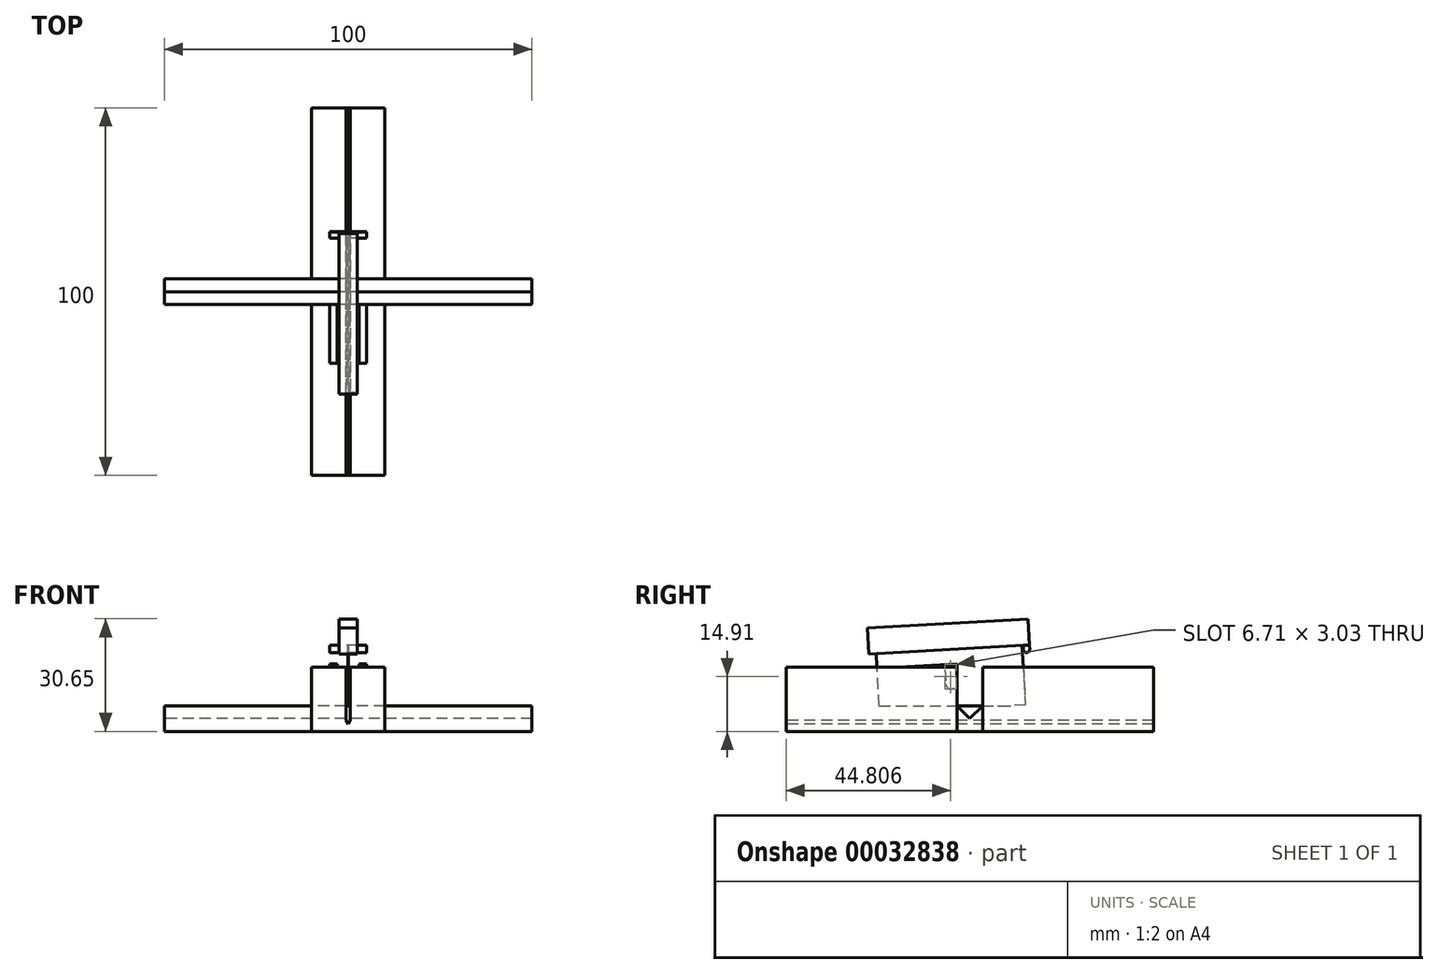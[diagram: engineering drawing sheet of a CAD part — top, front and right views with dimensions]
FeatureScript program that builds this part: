
annotation { "Feature Type Name" : "Feature", "Feature Type Description" : "" }
export const myFeature = defineFeature(function(context is Context, id is Id, definition is map)
    precondition{}
    {
        {
            var Q0;
            Q0=qCreatedBy(makeId("Right.planeOp"),FACE);
            var sketch = newSketch(context, id + "F0", { "sketchPlane" : qUnion([Q0])});
            skLineSegment(sketch, "E0.rect.bottom", {"start": v(3.5, 3.5) * mm, "end": v(-3.5, 3.5) * mm});
            skLineSegment(sketch, "E0.rect.top", {"start": v(3.5, -3.5) * mm, "end": v(-3.5, -3.5) * mm});
            skLineSegment(sketch, "E0.rect.left", {"start": v(3.5, 3.5) * mm, "end": v(3.5, -3.5) * mm});
            skLineSegment(sketch, "E0.rect.right", {"start": v(-3.5, 3.5) * mm, "end": v(-3.5, -3.5) * mm});
            skPoint(sketch, "E0.rect.middle", {"position": v(0, 0) * mm});
            skLineSegment(sketch, "E1", {"start": v(3.5, 3.5) * mm, "end": v(0, 0) * mm});
            skLineSegment(sketch, "E2", {"start": v(-3.5, 3.5) * mm, "end": v(0, 0) * mm});
            skCircle(sketch, "E3", {"center": v(0, 1.68) * mm, "radius": 1.2 * mm, "construction": true});
            skCircle(sketch, "E4", {"center": v(0, 3.54) * mm, "radius": 2.5 * mm, "construction": true});
            skSolve(sketch);
        }
        {
            var Q0;
            Q0=makeQuery(id+"F0.imprint","IMPRINT",FACE,{"disambiguationData":[TD([[makeQuery(id+"F0.imprint","IMPRINT",EDGE,{"derivedFrom":sQuery(id+"F0.wireOp",EDGE,"E0.rect.top")}),-1.0]])]});
            extrude(context, id + "F1", {"entities" : qUnion([Q0]), "endBound" : BoundingType.SYMMETRIC, "depth" : 100 * mm});
        }
        {
            var Q0;
            Q0=qCreatedBy(makeId("Front.planeOp"),FACE);
            var sketch = newSketch(context, id + "F2", { "sketchPlane" : qUnion([Q0])});
            skLineSegment(sketch, "E5.0", {"start": v(50, -3.5) * mm, "end": v(-50, -3.5) * mm});
            skLineSegment(sketch, "E6.bottom", {"start": v(-34.76, -3.5) * mm, "end": v(-25.26, -3.5) * mm});
            skLineSegment(sketch, "E6.top", {"start": v(-34.76, 13.07) * mm, "end": v(-25.26, 13.07) * mm});
            skLineSegment(sketch, "E6.left", {"start": v(-34.76, -3.5) * mm, "end": v(-34.76, 13.07) * mm});
            skLineSegment(sketch, "E6.right", {"start": v(-25.26, -3.5) * mm, "end": v(-25.26, 13.07) * mm});
            skSolve(sketch);
        }
        {
            var Q0;
            Q0=qCreatedBy(makeId("Right.planeOp"),FACE);
            var sketch = newSketch(context, id + "F3", { "sketchPlane" : qUnion([Q0])});
            skLineSegment(sketch, "E7", {"start": v(-24.54, 1.5) * mm, "end": v(-25.62, 20.82) * mm});
            skLineSegment(sketch, "E8", {"start": v(-25.62, 20.82) * mm, "end": v(14.06, 23.04) * mm});
            skLineSegment(sketch, "E9", {"start": v(14.06, 23.04) * mm, "end": v(15.14, 3.72) * mm});
            skLineSegment(sketch, "E10", {"start": v(15.14, 3.72) * mm, "end": v(-24.54, 1.5) * mm});
            skLineSegment(sketch, "E11", {"start": v(-24.54, 1.5) * mm, "end": v(25.1, 1.5) * mm});
            skCircle(sketch, "E12", {"center": v(-5.3, 13.36) * mm, "radius": 1.41 * mm});
            skCircle(sketch, "E13", {"center": v(-5.09, 9.46) * mm, "radius": 1.41 * mm});
            skLineSegment(sketch, "E14", {"start": v(-6.71, 13.28) * mm, "end": v(-6.5, 9.38) * mm});
            skLineSegment(sketch, "E15", {"start": v(-3.9, 13.44) * mm, "end": v(-3.68, 9.54) * mm});
            skLineSegment(sketch, "E16", {"start": v(-5.78, 21.93) * mm, "end": v(-4.7, 2.61) * mm, "construction": true});
            skLineSegment(sketch, "E17", {"start": v(-27.84, 24.7) * mm, "end": v(-27.44, 17.58) * mm});
            skLineSegment(sketch, "E18", {"start": v(-27.44, 17.58) * mm, "end": v(16.23, 20.03) * mm});
            skLineSegment(sketch, "E19", {"start": v(16.23, 20.03) * mm, "end": v(15.83, 27.15) * mm});
            skLineSegment(sketch, "E20", {"start": v(15.83, 27.15) * mm, "end": v(-27.84, 24.7) * mm});
            skSolve(sketch);
        }
        {
            var Q0;
            {var subQ9=sQuery(id+"F3.wireOp",EDGE,"E10");Q0=makeQuery(id+"F3.imprint","IMPRINT",FACE,{"disambiguationData":[TD([[makeQuery(id+"F3.imprint","IMPRINT",EDGE,{"derivedFrom":subQ9}),-1.0]])]});}
            extrude(context, id + "F4", {"entities" : qUnion([Q0]), "endBound" : BoundingType.SYMMETRIC, "depth" : .22 * mm});
        }
        {
            var Q0;
            {var subQ5=sQuery(id+"F3.wireOp",EDGE,"E8");Q0=makeQuery(id+"F3.imprint","IMPRINT",FACE,{"disambiguationData":[TD([[makeQuery(id+"F3.imprint","IMPRINT",EDGE,{"derivedFrom":subQ5}),-1.0]])]});}
            extrude(context, id + "F5", {"entities" : qUnion([Q0]), "operationType" : NewBodyOperationType.ADD, "endBound" : BoundingType.SYMMETRIC, "depth" : 1.15 * mm});
        }
        {
            var Q0;
            {var subQ7=sQuery(id+"F3.wireOp",EDGE,"E8");Q0=makeQuery(id+"F3.imprint","IMPRINT",FACE,{"disambiguationData":[TD([[makeQuery(id+"F3.imprint","IMPRINT",EDGE,{"derivedFrom":subQ7}),1.0]])]});}
            extrude(context, id + "F6", {"entities" : qUnion([Q0]), "endBound" : BoundingType.SYMMETRIC, "depth" : 5 * mm});
        }
        {
            var Q0;
            Q0=makeQuery(id+"F5.opExtrude","CAP_FACE",FACE,{"disambiguationData":[OSD([sQuery(id+"F3.wireOp",EDGE,"E7"),sQuery(id+"F3.wireOp",EDGE,"E8"),sQuery(id+"F3.wireOp",EDGE,"E9"),sQuery(id+"F3.wireOp",EDGE,"E18")])],"isStart":true});
            var Q1;
            Q1=makeQuery(id+"F6.opExtrude","CAP_FACE",FACE,{"disambiguationData":[OSD([sQuery(id+"F3.wireOp",EDGE,"E7"),sQuery(id+"F3.wireOp",EDGE,"E8"),sQuery(id+"F3.wireOp",EDGE,"E9"),sQuery(id+"F3.wireOp",EDGE,"E17"),sQuery(id+"F3.wireOp",EDGE,"E18"),sQuery(id+"F3.wireOp",EDGE,"E19"),sQuery(id+"F3.wireOp",EDGE,"E20")])],"isStart":true});
            extrude(context, id + "F7", {"entities" : qUnion([Q0]), "operationType" : NewBodyOperationType.ADD, "endBound" : BoundingType.UP_TO_SURFACE, "endBoundEntityFace" : qUnion([Q1]), "depth" : 25 * mm});
        }
        {
            var Q0;
            Q0=makeQuery(id+"F5.opExtrude","CAP_FACE",FACE,{"disambiguationData":[OSD([sQuery(id+"F3.wireOp",EDGE,"E7"),sQuery(id+"F3.wireOp",EDGE,"E8"),sQuery(id+"F3.wireOp",EDGE,"E9"),sQuery(id+"F3.wireOp",EDGE,"E18")])],"isStart":false});
            var Q1;
            Q1=makeQuery(id+"F6.opExtrude","CAP_FACE",FACE,{"disambiguationData":[OSD([sQuery(id+"F3.wireOp",EDGE,"E7"),sQuery(id+"F3.wireOp",EDGE,"E8"),sQuery(id+"F3.wireOp",EDGE,"E9"),sQuery(id+"F3.wireOp",EDGE,"E17"),sQuery(id+"F3.wireOp",EDGE,"E18"),sQuery(id+"F3.wireOp",EDGE,"E19"),sQuery(id+"F3.wireOp",EDGE,"E20")])],"isStart":false});
            extrude(context, id + "F8", {"entities" : qUnion([Q0]), "operationType" : NewBodyOperationType.ADD, "endBound" : BoundingType.UP_TO_SURFACE, "endBoundEntityFace" : qUnion([Q1]), "depth" : 25 * mm});
        }
        {
            var Q0;
            Q0=qCreatedBy(makeId("Front.planeOp"),FACE);
            var sketch = newSketch(context, id + "F9", { "sketchPlane" : qUnion([Q0])});
            skLineSegment(sketch, "E21.bottom", {"start": v(-0.61, 3.5) * mm, "end": v(0.6, 3.5) * mm});
            skLineSegment(sketch, "E21.top", {"start": v(-0.6, -1.5) * mm, "end": v(0.61, -1.5) * mm});
            skLineSegment(sketch, "E21.left", {"start": v(-0.61, 3.5) * mm, "end": v(-0.6, -1.5) * mm});
            skLineSegment(sketch, "E21.right", {"start": v(0.6, 3.5) * mm, "end": v(0.61, -1.5) * mm});
            skLineSegment(sketch, "E22", {"start": v(0, -1.5) * mm, "end": v(-0.6, -0.5) * mm});
            skLineSegment(sketch, "E23", {"start": v(0, -1.5) * mm, "end": v(0.61, -0.5) * mm});
            skSolve(sketch);
        }
        {
            var Q0;
            Q0=makeQuery(id+"F9.imprint","IMPRINT",FACE,{"disambiguationData":[TD([[makeQuery(id+"F9.imprint","IMPRINT",EDGE,{"derivedFrom":sQuery(id+"F9.wireOp",EDGE,"E21.bottom")}),-1.0]])]});
            var Q1;
            Q1=sQuery(id+"F9.wireOp",EDGE,"E21.left");
            extrude(context, id + "F10", {"entities" : qUnion([Q0]), "operationType" : NewBodyOperationType.REMOVE, "surfaceEntities" : qUnion([Q1]), "endBound" : BoundingType.THROUGH_ALL, "oppositeDirection" : true, "depth" : 25 * mm, "hasSecondDirection" : true, "secondDirectionBound" : SecondDirectionBoundingType.THROUGH_ALL, "secondDirectionOppositeDirection" : false, "secondDirectionDepth" : 25 * mm});
        }
        {
            var Q0;
            Q0=qCreatedBy(makeId("Right.planeOp"),FACE);
            var sketch = newSketch(context, id + "F11", { "sketchPlane" : qUnion([Q0])});
            skLineSegment(sketch, "E24.0", {"start": v(3.5, -0.5) * mm, "end": v(-3.5, -0.5) * mm});
            skLineSegment(sketch, "E25.bottom", {"start": v(50, -3.5) * mm, "end": v(-50, -3.5) * mm});
            skLineSegment(sketch, "E25.top", {"start": v(50, 1.5) * mm, "end": v(-50, 1.5) * mm});
            skLineSegment(sketch, "E25.left", {"start": v(50, -3.5) * mm, "end": v(50, 1.5) * mm});
            skLineSegment(sketch, "E25.right", {"start": v(-50, -3.5) * mm, "end": v(-50, 1.5) * mm});
            skLineSegment(sketch, "E26.0", {"start": v(3.5, 3.5) * mm, "end": v(0, 0) * mm});
            skLineSegment(sketch, "E26.1", {"start": v(-3.5, 3.5) * mm, "end": v(0, 0) * mm});
            skSolve(sketch);
        }
        {
            var Q0;
            Q0=makeQuery(id+"F11.imprint","IMPRINT",FACE,{"disambiguationData":[TD([[makeQuery(id+"F11.imprint","IMPRINT",EDGE,{"derivedFrom":sQuery(id+"F11.wireOp",EDGE,"E25.bottom")}),-1.0]])]});
            extrude(context, id + "F12", {"entities" : qUnion([Q0]), "operationType" : NewBodyOperationType.ADD, "endBound" : BoundingType.SYMMETRIC, "depth" : 20 * mm});
        }
        {
            var Q0;
            {var subQ3=sQuery(id+"F9.wireOp",EDGE,"E21.bottom");Q0=makeQuery(id+"F9.imprint","IMPRINT",FACE,{"disambiguationData":[TD([[makeQuery(id+"F9.imprint","IMPRINT",EDGE,{"derivedFrom":subQ3}),-1.0]])]});}
            extrude(context, id + "F13", {"entities" : qUnion([Q0]), "operationType" : NewBodyOperationType.REMOVE, "endBound" : BoundingType.THROUGH_ALL, "oppositeDirection" : true, "depth" : 25 * mm, "hasSecondDirection" : true, "secondDirectionBound" : SecondDirectionBoundingType.THROUGH_ALL, "secondDirectionOppositeDirection" : false, "secondDirectionDepth" : 25 * mm});
        }
        {
            var Q0;
            {var subQ0=sQuery(id+"F11.wireOp",EDGE,"E25.top");var subQ1=sQuery(id+"F9.wireOp",EDGE,"E21.right");var subQ2=sQuery(id+"F11.wireOp",EDGE,"E25.left");Q0=makeQuery(id+"F13.boolean.opBoolean","SPLIT",FACE,{"disambiguationData":[TD([makeQuery(id+"F1.opExtrude","SWEPT_FACE",FACE,{"disambiguationData":[OSD([sQuery(id+"F0.wireOp",EDGE,"E0.rect.left")])]}),makeQuery(id+"F10.boolean.opBoolean","COPY",FACE,{"derivedFrom":makeQuery(id+"F10.opExtrude","SWEPT_FACE",FACE,{"disambiguationData":[OSD([subQ1])]})}),makeQuery(id+"F12.opExtrude","CAP_FACE",FACE,{"disambiguationData":[OSD([sQuery(id+"F11.wireOp",EDGE,"E25.bottom"),subQ0,subQ2,sQuery(id+"F11.wireOp",EDGE,"E25.right")])],"isStart":false}),makeQuery(id+"F12.opExtrude","SWEPT_FACE",FACE,{"disambiguationData":[OSD([subQ2])]}),makeQuery(id+"F13.opExtrude","SWEPT_FACE",FACE,{"disambiguationData":[OSD([subQ1])]})])],"derivedFrom":makeQuery(id+"F12.opExtrude","SWEPT_FACE",FACE,{"disambiguationData":[OSD([subQ0])]})});}
            var Q1;
            {var subQ0=sQuery(id+"F11.wireOp",EDGE,"E25.top");var subQ1=sQuery(id+"F9.wireOp",EDGE,"E21.left");var subQ2=sQuery(id+"F11.wireOp",EDGE,"E25.left");Q1=makeQuery(id+"F13.boolean.opBoolean","SPLIT",FACE,{"disambiguationData":[TD([makeQuery(id+"F1.opExtrude","SWEPT_FACE",FACE,{"disambiguationData":[OSD([sQuery(id+"F0.wireOp",EDGE,"E0.rect.left")])]}),makeQuery(id+"F10.boolean.opBoolean","COPY",FACE,{"derivedFrom":makeQuery(id+"F10.opExtrude","SWEPT_FACE",FACE,{"disambiguationData":[OSD([subQ1])]})}),makeQuery(id+"F12.opExtrude","CAP_FACE",FACE,{"disambiguationData":[OSD([sQuery(id+"F11.wireOp",EDGE,"E25.bottom"),subQ0,subQ2,sQuery(id+"F11.wireOp",EDGE,"E25.right")])],"isStart":true}),makeQuery(id+"F12.opExtrude","SWEPT_FACE",FACE,{"disambiguationData":[OSD([subQ2])]}),makeQuery(id+"F13.opExtrude","SWEPT_FACE",FACE,{"disambiguationData":[OSD([subQ1])]})])],"derivedFrom":makeQuery(id+"F12.opExtrude","SWEPT_FACE",FACE,{"disambiguationData":[OSD([subQ0])]})});}
            var Q2;
            {var subQ0=sQuery(id+"F11.wireOp",EDGE,"E25.top");var subQ1=sQuery(id+"F9.wireOp",EDGE,"E21.left");var subQ2=sQuery(id+"F11.wireOp",EDGE,"E25.right");Q2=makeQuery(id+"F13.boolean.opBoolean","SPLIT",FACE,{"disambiguationData":[TD([makeQuery(id+"F1.opExtrude","SWEPT_FACE",FACE,{"disambiguationData":[OSD([sQuery(id+"F0.wireOp",EDGE,"E0.rect.right")])]}),makeQuery(id+"F10.boolean.opBoolean","COPY",FACE,{"derivedFrom":makeQuery(id+"F10.opExtrude","SWEPT_FACE",FACE,{"disambiguationData":[OSD([subQ1])]})}),makeQuery(id+"F12.opExtrude","CAP_FACE",FACE,{"disambiguationData":[OSD([sQuery(id+"F11.wireOp",EDGE,"E25.bottom"),subQ0,sQuery(id+"F11.wireOp",EDGE,"E25.left"),subQ2])],"isStart":true}),makeQuery(id+"F12.opExtrude","SWEPT_FACE",FACE,{"disambiguationData":[OSD([subQ2])]}),makeQuery(id+"F13.opExtrude","SWEPT_FACE",FACE,{"disambiguationData":[OSD([subQ1])]})])],"derivedFrom":makeQuery(id+"F12.opExtrude","SWEPT_FACE",FACE,{"disambiguationData":[OSD([subQ0])]})});}
            var Q3;
            {var subQ0=sQuery(id+"F11.wireOp",EDGE,"E25.top");var subQ1=sQuery(id+"F9.wireOp",EDGE,"E21.right");var subQ2=sQuery(id+"F11.wireOp",EDGE,"E25.right");Q3=makeQuery(id+"F13.boolean.opBoolean","SPLIT",FACE,{"disambiguationData":[TD([makeQuery(id+"F1.opExtrude","SWEPT_FACE",FACE,{"disambiguationData":[OSD([sQuery(id+"F0.wireOp",EDGE,"E0.rect.right")])]}),makeQuery(id+"F10.boolean.opBoolean","COPY",FACE,{"derivedFrom":makeQuery(id+"F10.opExtrude","SWEPT_FACE",FACE,{"disambiguationData":[OSD([subQ1])]})}),makeQuery(id+"F12.opExtrude","CAP_FACE",FACE,{"disambiguationData":[OSD([sQuery(id+"F11.wireOp",EDGE,"E25.bottom"),subQ0,sQuery(id+"F11.wireOp",EDGE,"E25.left"),subQ2])],"isStart":false}),makeQuery(id+"F12.opExtrude","SWEPT_FACE",FACE,{"disambiguationData":[OSD([subQ2])]}),makeQuery(id+"F13.opExtrude","SWEPT_FACE",FACE,{"disambiguationData":[OSD([subQ1])]})])],"derivedFrom":makeQuery(id+"F12.opExtrude","SWEPT_FACE",FACE,{"disambiguationData":[OSD([subQ0])]})});}
            extrude(context, id + "F14", {"entities" : qUnion([Q0, Q1, Q2, Q3]), "operationType" : NewBodyOperationType.ADD, "depth" : 12.5 * mm});
        }
        {
            var Q0;
            Q0=qCreatedBy(makeId("Right.planeOp"),FACE);
            var sketch = newSketch(context, id + "F15", { "sketchPlane" : qUnion([Q0])});
            skLineSegment(sketch, "E27.0", {"start": v(-27.44, 17.58) * mm, "end": v(16.23, 20.03) * mm});
            skLineSegment(sketch, "E28", {"start": v(16.34, 18.03) * mm, "end": v(14.65, 17.93) * mm});
            skLineSegment(sketch, "E29", {"start": v(14.65, 17.93) * mm, "end": v(14.54, 19.93) * mm});
            skLineSegment(sketch, "E30", {"start": v(16.34, 18.03) * mm, "end": v(16.23, 20.03) * mm});
            skCircle(sketch, "E31", {"center": v(15.45, 18.82) * mm, "radius": 0.84 * mm});
            skSolve(sketch);
        }
        {
            var Q0;
            {var subQ1=sQuery(id+"F15.wireOp",EDGE,"E30");var subQ5=sQuery(id+"F15.wireOp",EDGE,"E27.0");var subQ6=makeQuery(id+"F15.imprint","INTERSECT",VERTEX,{"derivedFrom":[subQ5,subQ1]});Q0=makeQuery(id+"F15.imprint","IMPRINT",FACE,{"disambiguationData":[TD([[makeQuery(id+"F15.imprint","IMPRINT",EDGE,{"disambiguationData":[TD([[subQ6,1.0]])],"derivedFrom":subQ5}),-1.0]])]});}
            var Q1;
            {var subQ0=sQuery(id+"F15.wireOp",EDGE,"E31");var subQ3=makeQuery(id+"F15.imprint","INTERSECT",VERTEX,{"derivedFrom":[sQuery(id+"F15.wireOp",EDGE,"E29"),subQ0]});Q1=makeQuery(id+"F15.imprint","IMPRINT",FACE,{"disambiguationData":[TD([[makeQuery(id+"F15.imprint","IMPRINT",EDGE,{"disambiguationData":[TD([[subQ3,1.0]])],"derivedFrom":subQ0}),1.0]])]});}
            extrude(context, id + "F16", {"entities" : qUnion([Q0, Q1]), "operationType" : NewBodyOperationType.ADD, "endBound" : BoundingType.SYMMETRIC, "depth" : 10 * mm});
        }
        {
            var Q0;
            Q0=qCreatedBy(makeId("Right.planeOp"),FACE);
            cPlane(context, id + "F17", {"entities" : qUnion([Q0]), "cplaneType" : CPlaneType.OFFSET, "offset" : 3 * mm, "width" : 150 * mm, "height" : 150 * mm});
        }
        {
            var Q0;
            Q0=qCreatedBy(id+"F17.planeOp",FACE);
            var sketch = newSketch(context, id + "F18", { "sketchPlane" : qUnion([Q0])});
            skLineSegment(sketch, "E32", {"start": v(-19.44, 14) * mm, "end": v(-3.5, 14.9) * mm});
            skLineSegment(sketch, "E33.0", {"start": v(-3.5, 14) * mm, "end": v(-50, 14) * mm});
            skLineSegment(sketch, "E34", {"start": v(-3.5, 14.9) * mm, "end": v(-3.5, 14) * mm});
            skSolve(sketch);
        }
        {
            var Q0;
            Q0 = qSketchRegion(id + "F18", true);
            var Q1;
            Q1=makeQuery(id+"F16.opExtrude","CAP_FACE",FACE,{"disambiguationData":[OSD([sQuery(id+"F15.wireOp",EDGE,"E27.0"),sQuery(id+"F15.wireOp",EDGE,"E29"),sQuery(id+"F15.wireOp",EDGE,"E30"),sQuery(id+"F15.wireOp",EDGE,"E31")])],"isStart":false});
            extrude(context, id + "F19", {"entities" : qUnion([Q0]), "endBound" : BoundingType.UP_TO_SURFACE, "endBoundEntityFace" : qUnion([Q1]), "depth" : 25 * mm});
        }
        {
            var Q0;
            Q0=makeQuery(id+"F19.opExtrude","SWEPT_BODY",BODY,{"disambiguationData":[OSD([sQuery(id+"F18.wireOp",EDGE,"E32"),sQuery(id+"F18.wireOp",EDGE,"E33.0"),sQuery(id+"F18.wireOp",EDGE,"E34")])]});
            var Q1;
            Q1=qCreatedBy(makeId("Right.planeOp"),FACE);
            mirror(context, id + "F20", {"operationType" : NewBodyOperationType.ADD, "entities" : qUnion([Q0]), "mirrorPlane" : qUnion([Q1])});
        }
    });
